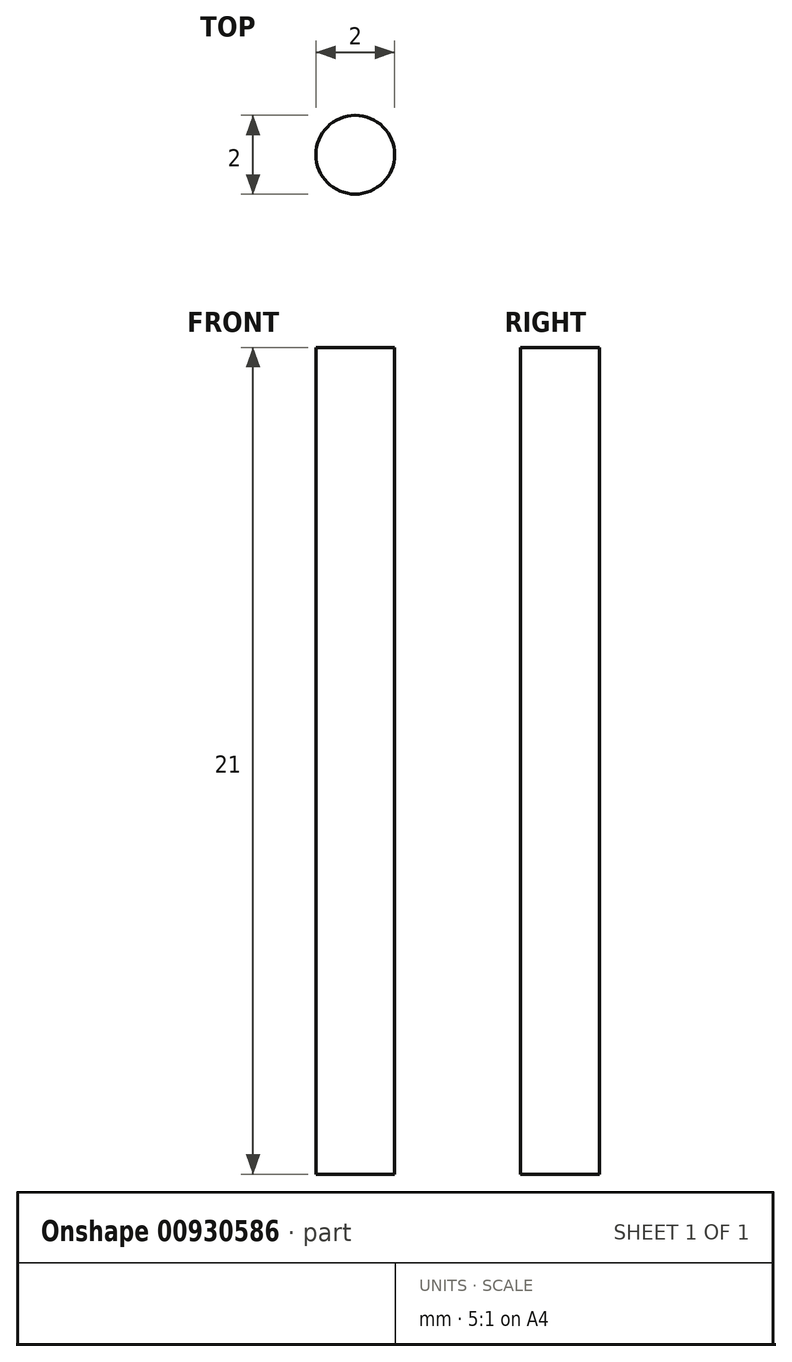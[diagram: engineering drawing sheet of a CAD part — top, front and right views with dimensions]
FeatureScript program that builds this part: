
annotation { "Feature Type Name" : "Feature", "Feature Type Description" : "" }
export const myFeature = defineFeature(function(context is Context, id is Id, definition is map)
    precondition{}
    {
        {
            var Q0;
            Q0=qCreatedBy(makeId("Top.planeOp"),FACE);
            var sketch = newSketch(context, id + "F0", { "sketchPlane" : qUnion([Q0])});
            skCircle(sketch, "E0", {"center": v(0, 0) * mm, "radius": 1 * mm});
            skSolve(sketch);
        }
        {
            var Q0;
            Q0=qSketchRegion(id+"F0",true);
            extrude(context, id + "F1", {"entities" : qUnion([Q0]), "depth" : 21 * mm});
        }
    });
